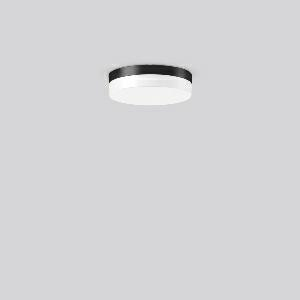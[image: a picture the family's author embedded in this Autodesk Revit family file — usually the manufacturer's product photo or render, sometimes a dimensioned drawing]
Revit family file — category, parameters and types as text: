
# Revit family: flat_slim_round_312132_0031_76_da21
name_source: partatom
category: Lighting Fixtures
units: mm (PartAtom-declared; Revit-internal decimal feet)

## family parameters
Cut with Voids When Loaded = No
Host = Face
Light Source = No
Part Type = Normal
Room Calculation Point = No
Round Connector Dimension = Use Diameter
Shared = No

## types (1)
- FLAT SLIM round (1 x LED Modul 830, 1000 lm, 3000)
    Apparent Load = 12 VA
    CIE Flux Codes = 42 72 91 89 100
    Color Rendering = 80
    Color Temperature = 3000
    Default Elevation = 1800 mm
    Height = 63 mm
    Lamp = 1 x LED Modul 830
    Lamp Light Flux = 1000 lm
    Lamp count = 1
    Length = 230 mm
    Lifetime = 50000 h
    Luminous efficacy = 83 lm/W
    Manufacturer = RZB
    ModVariant = No
    Model = 312132.0031.76
    Mounting Place = Ceiling, Wall
    Mounting Type = Surface mounted
    Number of Poles = 1
    OnlyDefault = Yes
    Power Factor = 1
    Product Name = FLAT SLIM round
    Product group = Surface mounted ceiling and wall luminaires
    ProductGroupID = 305
    Protection Class = Protection class I
    Protection Degree = IP 65
    RLX_Detail_Level = 1
    RLX_Emergency_Light_Flux = 0 lm
    RLX_Emergency_Type = 0
    RLX_Emergency_Type_DB = No
    RlxData = <blob elided: 17865 chars, md5=4c18e930>
    Socket = socket
    Standby Power = 0 W
    System Light Flux = 1000 lm
    System Power = 12 W
    Type Comments = Product without accessories
    Type Image = 312132.0031.jpg
    URL = http://relux.com
    VarID = ---
    Voltage = 230 V
    Voltage Range = 220-240 V
    Weight = 0.00 kg
    Width = 0 mm  [stored 0 ft]

note: [stored X ft] marks values corroborated as IEEE doubles in the binary element streams (Revit-internal decimal feet)

## geometry (parser evidence)
native form markers: Blend x4, Sweep x13
no freeform markers — native parametric forms only
